# Revit family: Chair_Task_Humanscale_DiffrientWorld
name_source: partatom
category: Furniture
units: mm (PartAtom-declared; Revit-internal decimal feet)

## family parameters
Always vertical = Yes
Cut with Voids When Loaded = No
OmniClass Number = 23.21.13.00
OmniClass Title = Retail and Office Equipment and Furnishings
Room Calculation Point = No
Shared = No
Work Plane-Based = No

## types (2) — shared parameters
Assembly Code = E2020200
Description = Designer Niels Diffrient wanted to create the most minimal, full-function task chair ever made. With an innovative tri-panel mesh backrest that provides custom back and lumbar support and a lightweight design, Humanscale’s Diffrient World is simple, beautiful and functional.
IfcExportAs = IfcFurniture
IfcExportType = CHAIR
Manufacturer = Schiavello
ManufacturerOverallDepth = 464 mm
ManufacturerURLProductSpecific = https://www.schiavello.com
ModifiedIssue = 20230127 $
URL = https://www.schiavello.com
Uniclass2015Code = Pr_40_50_12_57
Uniclass2015Title = Office chairs
Uniclass2015Version = Products v1.24

## per-type parameters (varying)
| type | ArmRest | ManufacturerOverallWidth | ManufacturerSpecCode | Model | NoArmRest | Type Comments |
| 533w x 464d x 940h_No Arm | No | 533 mm | Diffrient World Chair - 533w x 464d x 940h - No Arm | Diffrient World Chair - 533w x 464d x 940h - No Arm | Yes | 533w x 464d x 940h - No Arm |
| 635w x 464d x 940h_With Arm | Yes | 635 mm  [stored 2.08333 ft] | Diffrient World Chair - 635w x 464d x 940h - With Arm | Diffrient World Chair - 635w x 464d x 940h - With Arm | No | 635w x 464d x 940h - With Arm |

note: [stored X ft] marks values corroborated as IEEE doubles in the binary element streams (Revit-internal decimal feet)

## geometry (parser evidence)
native form markers: Sweep x5
no freeform markers — native parametric forms only
